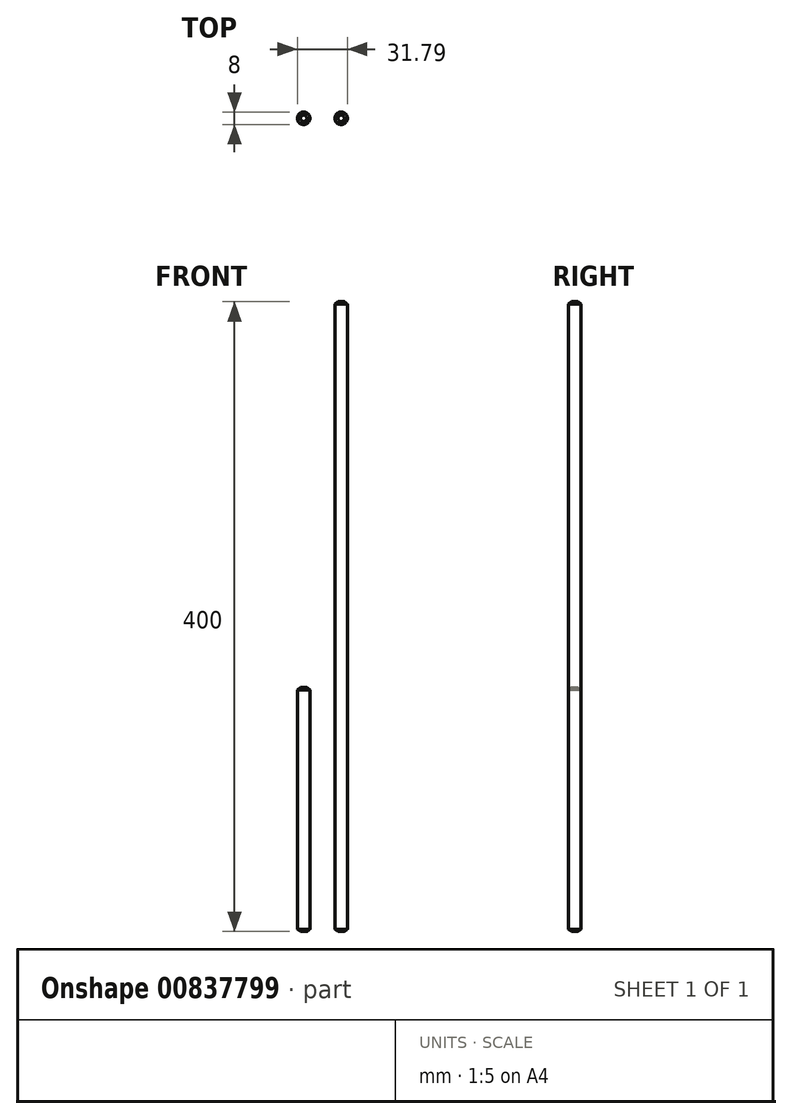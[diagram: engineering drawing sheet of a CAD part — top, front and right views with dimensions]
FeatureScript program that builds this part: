
annotation { "Feature Type Name" : "Feature", "Feature Type Description" : "" }
export const myFeature = defineFeature(function(context is Context, id is Id, definition is map)
    precondition{}
    {
        {
            var Q0;
            Q0=qCreatedBy(makeId("Top.planeOp"),FACE);
            var sketch = newSketch(context, id + "F0", { "sketchPlane" : qUnion([Q0])});
            skCircle(sketch, "E0", {"center": v(0, 0) * mm, "radius": 4 * mm});
            skCircle(sketch, "E1", {"center": v(-23.79, 0) * mm, "radius": 4 * mm});
            skSolve(sketch);
        }
        {
            var Q0;
            Q0=makeQuery(id+"F0.imprint","IMPRINT",FACE,{"disambiguationData":[TD([[makeQuery(id+"F0.imprint","IMPRINT",EDGE,{"derivedFrom":sQuery(id+"F0.wireOp",EDGE,"E0")}),1.0]])]});
            extrude(context, id + "F1", {"entities" : qUnion([Q0]), "depth" : 400 * mm, "offsetDistance" : 25 * mm});
        }
        {
            var Q0;
            Q0=makeQuery(id+"F1.opExtrude","CAP_EDGE",EDGE,{"disambiguationData":[OSD([sQuery(id+"F0.wireOp",EDGE,"E0")])],"isStart":true});
            var Q1;
            Q1=makeQuery(id+"F1.opExtrude","CAP_EDGE",EDGE,{"disambiguationData":[OSD([sQuery(id+"F0.wireOp",EDGE,"E0")])],"isStart":false});
            chamfer(context, id + "F2", {"entities" : qUnion([Q0, Q1]), "chamferType" : ChamferType.TWO_OFFSETS, "width1" : 1.5 * mm, "oppositeDirection" : false, "width2" : 2 * mm, "tangentPropagation" : true});
        }
        {
            var Q0;
            Q0=makeQuery(id+"F0.imprint","IMPRINT",FACE,{"disambiguationData":[TD([[makeQuery(id+"F0.imprint","IMPRINT",EDGE,{"derivedFrom":sQuery(id+"F0.wireOp",EDGE,"E1")}),1.0]])]});
            extrude(context, id + "F3", {"entities" : qUnion([Q0]), "depth" : 155 * mm, "offsetDistance" : 25 * mm});
        }
        {
            var Q0;
            Q0=makeQuery(id+"F3.opExtrude","CAP_EDGE",EDGE,{"disambiguationData":[OSD([sQuery(id+"F0.wireOp",EDGE,"E1")])],"isStart":false});
            var Q1;
            Q1=makeQuery(id+"F3.opExtrude","CAP_EDGE",EDGE,{"disambiguationData":[OSD([sQuery(id+"F0.wireOp",EDGE,"E1")])],"isStart":true});
            chamfer(context, id + "F4", {"entities" : qUnion([Q0, Q1]), "chamferType" : ChamferType.TWO_OFFSETS, "width1" : 1.5 * mm, "oppositeDirection" : true, "width2" : 2 * mm, "tangentPropagation" : true});
        }
    });
